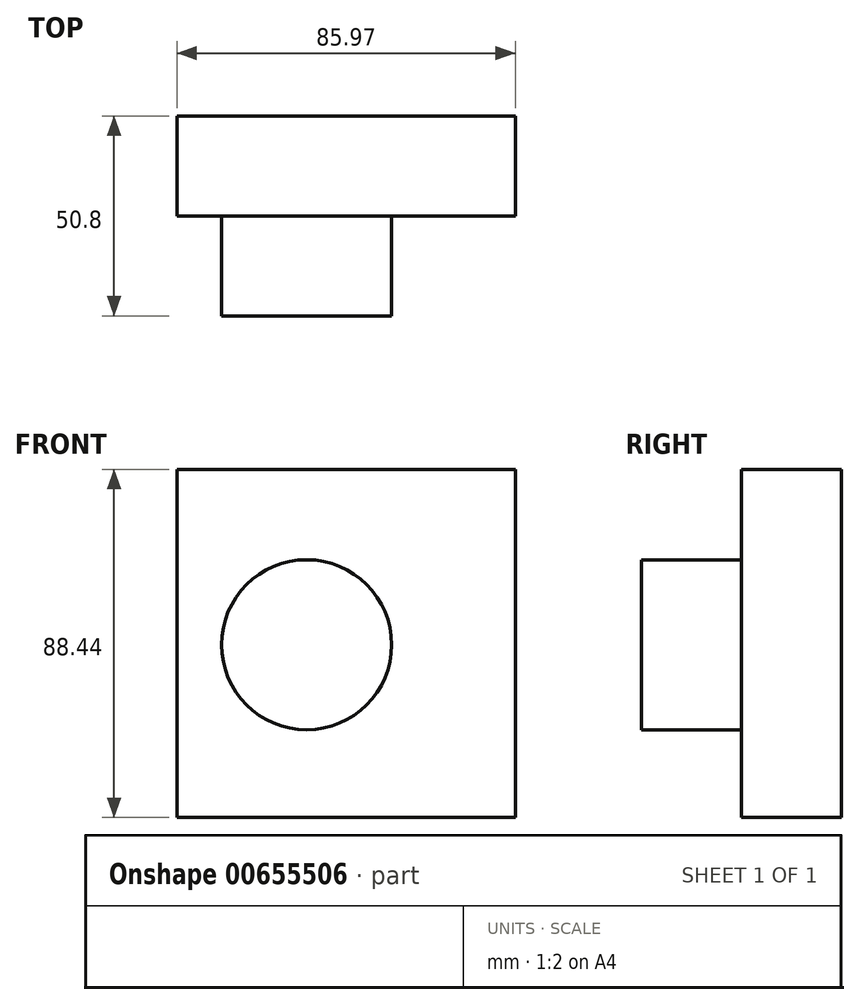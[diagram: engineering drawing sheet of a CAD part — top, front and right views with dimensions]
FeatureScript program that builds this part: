
annotation { "Feature Type Name" : "Feature", "Feature Type Description" : "" }
export const myFeature = defineFeature(function(context is Context, id is Id, definition is map)
    precondition{}
    {
        {
            var Q0;
            Q0=qCreatedBy(makeId("Front.planeOp"),FACE);
            var sketch = newSketch(context, id + "F0", { "sketchPlane" : qUnion([Q0])});
            skLineSegment(sketch, "E0.bottom", {"start": v(-56.88, 50.76) * mm, "end": v(29.09, 50.76) * mm});
            skLineSegment(sketch, "E0.top", {"start": v(-56.88, -37.68) * mm, "end": v(29.09, -37.68) * mm});
            skLineSegment(sketch, "E0.left", {"start": v(-56.88, 50.76) * mm, "end": v(-56.88, -37.68) * mm});
            skLineSegment(sketch, "E0.right", {"start": v(29.09, 50.76) * mm, "end": v(29.09, -37.68) * mm});
            skSolve(sketch);
        }
        {
            var Q0;
            Q0 = qSketchRegion(id + "F0", true);
            extrude(context, id + "F1", {"entities" : qUnion([Q0]), "oppositeDirection" : true, "depth" : 25.4 * mm, "offsetDistance" : 25.4 * mm});
        }
        {
            var Q0;
            Q0=makeQuery(id+"F1.opExtrude","CAP_FACE",FACE,{"disambiguationData":[OSD([sQuery(id+"F0.wireOp",EDGE,"E0.bottom"),sQuery(id+"F0.wireOp",EDGE,"E0.top"),sQuery(id+"F0.wireOp",EDGE,"E0.left"),sQuery(id+"F0.wireOp",EDGE,"E0.right")])],"isStart":true});
            var sketch = newSketch(context, id + "F2", { "sketchPlane" : qUnion([Q0])});
            skCircle(sketch, "E1", {"center": v(-23.94, 6.22) * mm, "radius": 21.6 * mm});
            skSolve(sketch);
        }
        {
            var Q0;
            Q0 = qSketchRegion(id + "F2", true);
            extrude(context, id + "F3", {"entities" : qUnion([Q0]), "operationType" : NewBodyOperationType.ADD, "depth" : 25.4 * mm, "offsetDistance" : 25.4 * mm});
        }
    });
